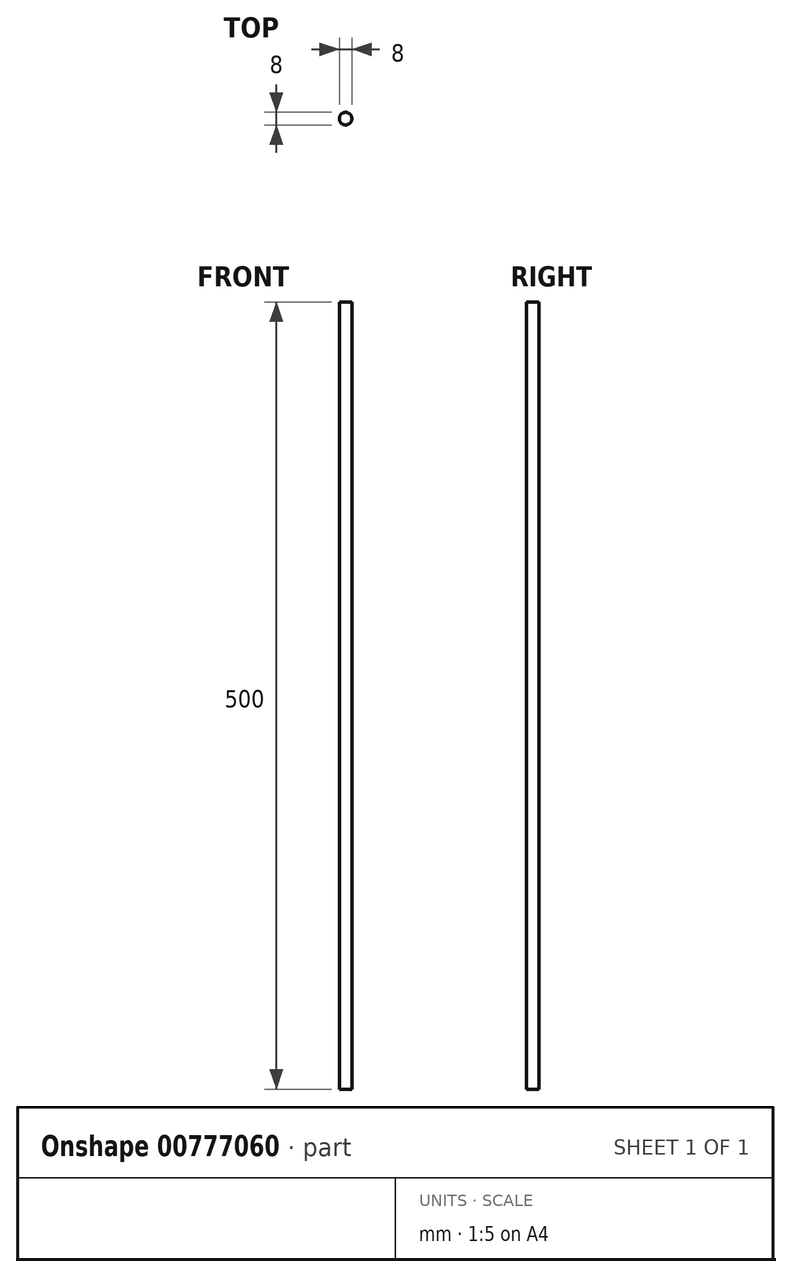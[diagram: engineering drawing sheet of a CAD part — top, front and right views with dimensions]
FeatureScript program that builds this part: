
annotation { "Feature Type Name" : "Feature", "Feature Type Description" : "" }
export const myFeature = defineFeature(function(context is Context, id is Id, definition is map)
    precondition{}
    {
        {
            var Q0;
            Q0=qCreatedBy(makeId("Top.planeOp"),FACE);
            var sketch = newSketch(context, id + "F0", { "sketchPlane" : qUnion([Q0])});
            skCircle(sketch, "E0", {"center": v(0, 0) * mm, "radius": 4 * mm});
            skSolve(sketch);
        }
        {
            var Q0;
            Q0=qSketchRegion(id+"F0",true);
            extrude(context, id + "F1", {"entities" : qUnion([Q0]), "depth" : 500 * mm, "offsetDistance" : 25 * mm});
        }
    });
